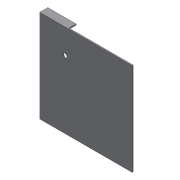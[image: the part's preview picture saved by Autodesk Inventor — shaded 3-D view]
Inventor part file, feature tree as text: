
AUTODESK INVENTOR PART (.ipt)
format: ipt  version: 2017 (Build 210142000, 142)  size: 141,312 bytes
history: native  units: mm
features: sketch x5, extrude x3, projected_geometry x3, hole x1
ambient origin geometry x8: Origin, YZ Plane, XZ Plane, XY Plane, X Axis, Y Axis, Z Axis, Center Point
bodies: Solid1 (feature_tree)
feature tree (12):
  extrude  "Extrusion1"  Depth=90.0mm
  sketch  "Sketch2"  dims[d2=92.0mm d3=92.0mm]
  extrude  "Extrusion2"  Depth=92.0mm
  extrude  "Extrusion3"  Depth=1.0mm
  hole  "Hole1"  [1 undecoded]
  sketch  "Sketch1"  dims[d0=90.0mm d1=90.0mm]
  projected_geometry  "Projected Loop1"
  sketch  "Sketch3"  dims[d4=1.0mm d5=0.0mm d6=90.0mm]
  sketch  "Sketch4"  dims[d7=90.0mm d8=1.0mm]
  projected_geometry  "Projected Loop2"
  projected_geometry  "Projected Loop3"
  sketch  "Sketch5"  dims[d9=1.0mm d10=10.0mm d11=10.0mm d12=14.5mm d13=17.25mm d14=7.0mm d15=0.0mm d16=22.5mm d17=8.625mm d18=10.0mm d19=0.0mm d23=25.0mm d24=25.0mm d25=4.0mm d26=6.0mm d27=4.0mm d28=2.0mm d29=90.0deg d30=8.0mm d31=20.594885mm]
note: 1 required parameter value undecoded (feature->parameter linkage not recoverable at this tier; creation-order binding heuristic only, values carry confidence <= 0.55)
